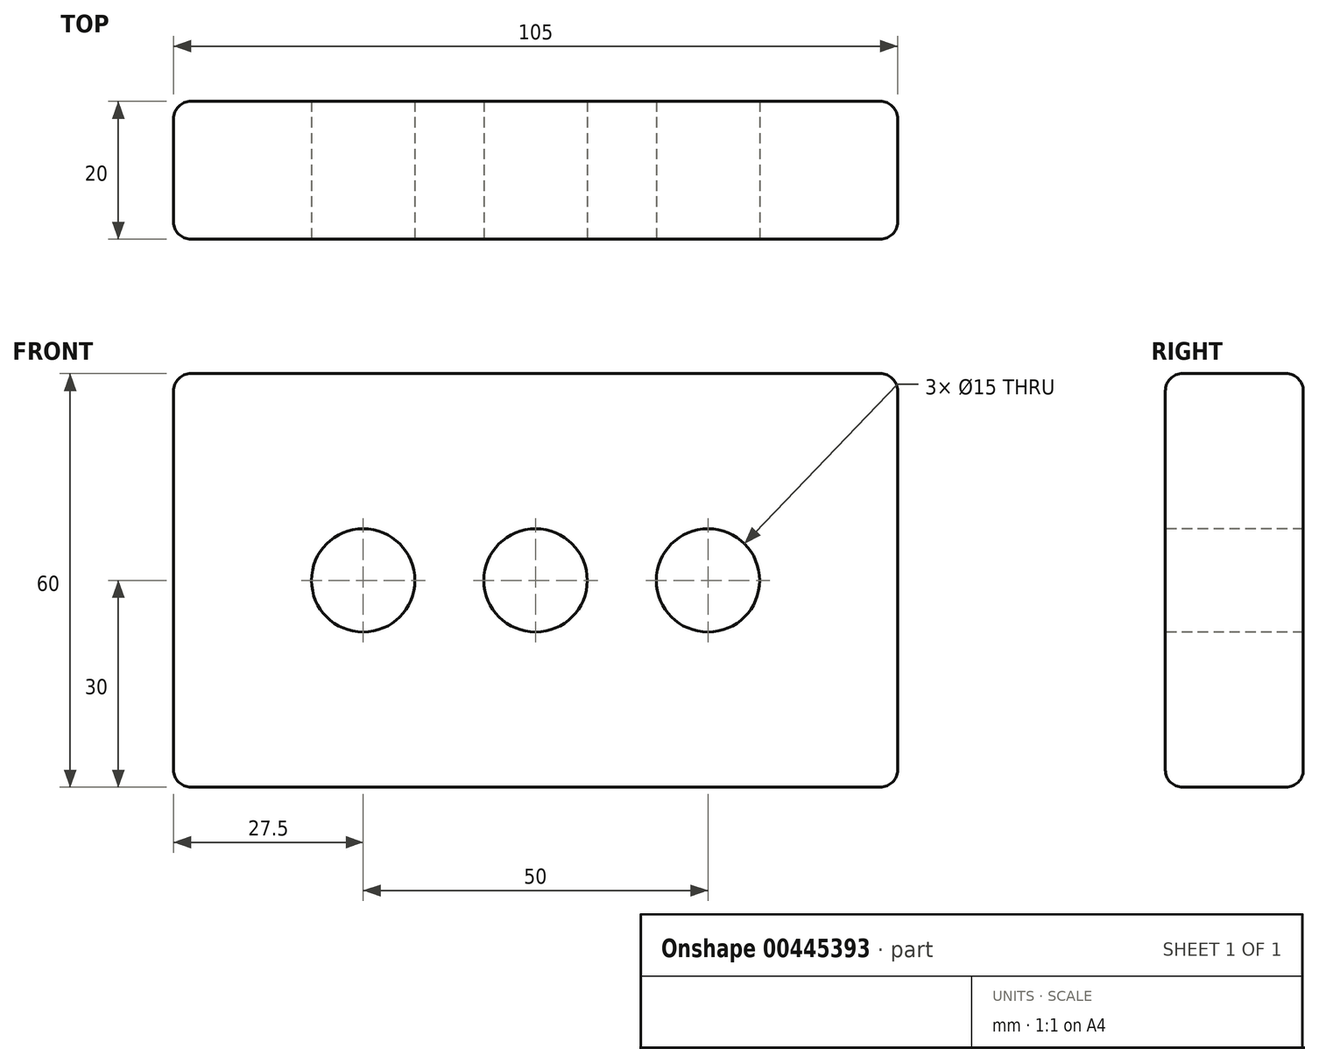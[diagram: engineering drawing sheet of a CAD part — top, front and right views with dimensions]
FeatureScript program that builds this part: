
annotation { "Feature Type Name" : "Feature", "Feature Type Description" : "" }
export const myFeature = defineFeature(function(context is Context, id is Id, definition is map)
    precondition{}
    {
        {
            var Q0;
            Q0=qCreatedBy(makeId("Front.planeOp"),FACE);
            var sketch = newSketch(context, id + "F0", { "sketchPlane" : qUnion([Q0])});
            skLineSegment(sketch, "E0.bottom", {"start": v(52.5, -30) * mm, "end": v(-52.5, -30) * mm});
            skLineSegment(sketch, "E0.top", {"start": v(52.5, 30) * mm, "end": v(-52.5, 30) * mm});
            skLineSegment(sketch, "E0.left", {"start": v(52.5, -30) * mm, "end": v(52.5, 30) * mm});
            skLineSegment(sketch, "E0.right", {"start": v(-52.5, -30) * mm, "end": v(-52.5, 30) * mm});
            skPoint(sketch, "E0.middle", {"position": v(0, 0) * mm});
            skSolve(sketch);
        }
        {
            var Q0;
            Q0=makeQuery(id+"F0.imprint","IMPRINT",FACE,{"disambiguationData":[TD([[makeQuery(id+"F0.imprint","IMPRINT",EDGE,{"derivedFrom":sQuery(id+"F0.wireOp",EDGE,"E0.bottom")}),-1.0]])]});
            extrude(context, id + "F1", {"entities" : qUnion([Q0]), "depth" : 20 * mm});
        }
        {
            var Q0;
            Q0=makeQuery(id+"F1.opExtrude","CAP_FACE",FACE,{"disambiguationData":[OSD([sQuery(id+"F0.wireOp",EDGE,"E0.bottom"),sQuery(id+"F0.wireOp",EDGE,"E0.top"),sQuery(id+"F0.wireOp",EDGE,"E0.left"),sQuery(id+"F0.wireOp",EDGE,"E0.right")])],"isStart":false});
            var sketch = newSketch(context, id + "F2", { "sketchPlane" : qUnion([Q0])});
            skCircle(sketch, "E1", {"center": v(0, 0) * mm, "radius": 7.5 * mm});
            skLineSegment(sketch, "E2", {"start": v(7.5, 0) * mm, "end": v(25, 0) * mm});
            skLineSegment(sketch, "E3", {"start": v(-7.5, 0) * mm, "end": v(-25, 0) * mm});
            skCircle(sketch, "E4", {"center": v(-25, 0) * mm, "radius": 7.5 * mm});
            skCircle(sketch, "E5", {"center": v(25, 0) * mm, "radius": 7.5 * mm});
            skSolve(sketch);
        }
        {
            var Q0;
            Q0=makeQuery(id+"F2.imprint","IMPRINT",FACE,{"disambiguationData":[TD([[makeQuery(id+"F2.imprint","IMPRINT",EDGE,{"derivedFrom":sQuery(id+"F2.wireOp",EDGE,"E4")}),1.0]])]});
            var Q1;
            {var subQ0=sQuery(id+"F2.wireOp",EDGE,"E1");var subQ1=makeQuery(id+"F2.imprint","IMPRINT",VERTEX,{"disambiguationData":[OD(0.0)],"derivedFrom":subQ0});Q1=makeQuery(id+"F2.imprint","IMPRINT",FACE,{"disambiguationData":[TD([[makeQuery(id+"F2.imprint","IMPRINT",EDGE,{"disambiguationData":[TD([[subQ1,-1.0]])],"derivedFrom":subQ0}),1.0]])]});}
            var Q2;
            Q2=makeQuery(id+"F2.imprint","IMPRINT",FACE,{"disambiguationData":[TD([[makeQuery(id+"F2.imprint","IMPRINT",EDGE,{"derivedFrom":sQuery(id+"F2.wireOp",EDGE,"E5")}),1.0]])]});
            extrude(context, id + "F3", {"entities" : qUnion([Q0, Q1, Q2]), "operationType" : NewBodyOperationType.REMOVE, "oppositeDirection" : true, "depth" : 25 * mm});
        }
        {
            var Q0;
            Q0=makeQuery(id+"F1.opExtrude","SWEPT_FACE",FACE,{"disambiguationData":[OSD([sQuery(id+"F0.wireOp",EDGE,"E0.left")])]});
            var Q1;
            Q1=makeQuery(id+"F1.opExtrude","SWEPT_FACE",FACE,{"disambiguationData":[OSD([sQuery(id+"F0.wireOp",EDGE,"E0.top")])]});
            var Q2;
            Q2=makeQuery(id+"F1.opExtrude","SWEPT_FACE",FACE,{"disambiguationData":[OSD([sQuery(id+"F0.wireOp",EDGE,"E0.right")])]});
            var Q3;
            Q3=makeQuery(id+"F1.opExtrude","SWEPT_FACE",FACE,{"disambiguationData":[OSD([sQuery(id+"F0.wireOp",EDGE,"E0.bottom")])]});
            fillet(context, id + "F4", {"entities" : qUnion([Q0, Q1, Q2, Q3]), "radius" : 2.5 * mm, "tangentPropagation" : true, "allowEdgeOverflow" : false});
        }
    });
